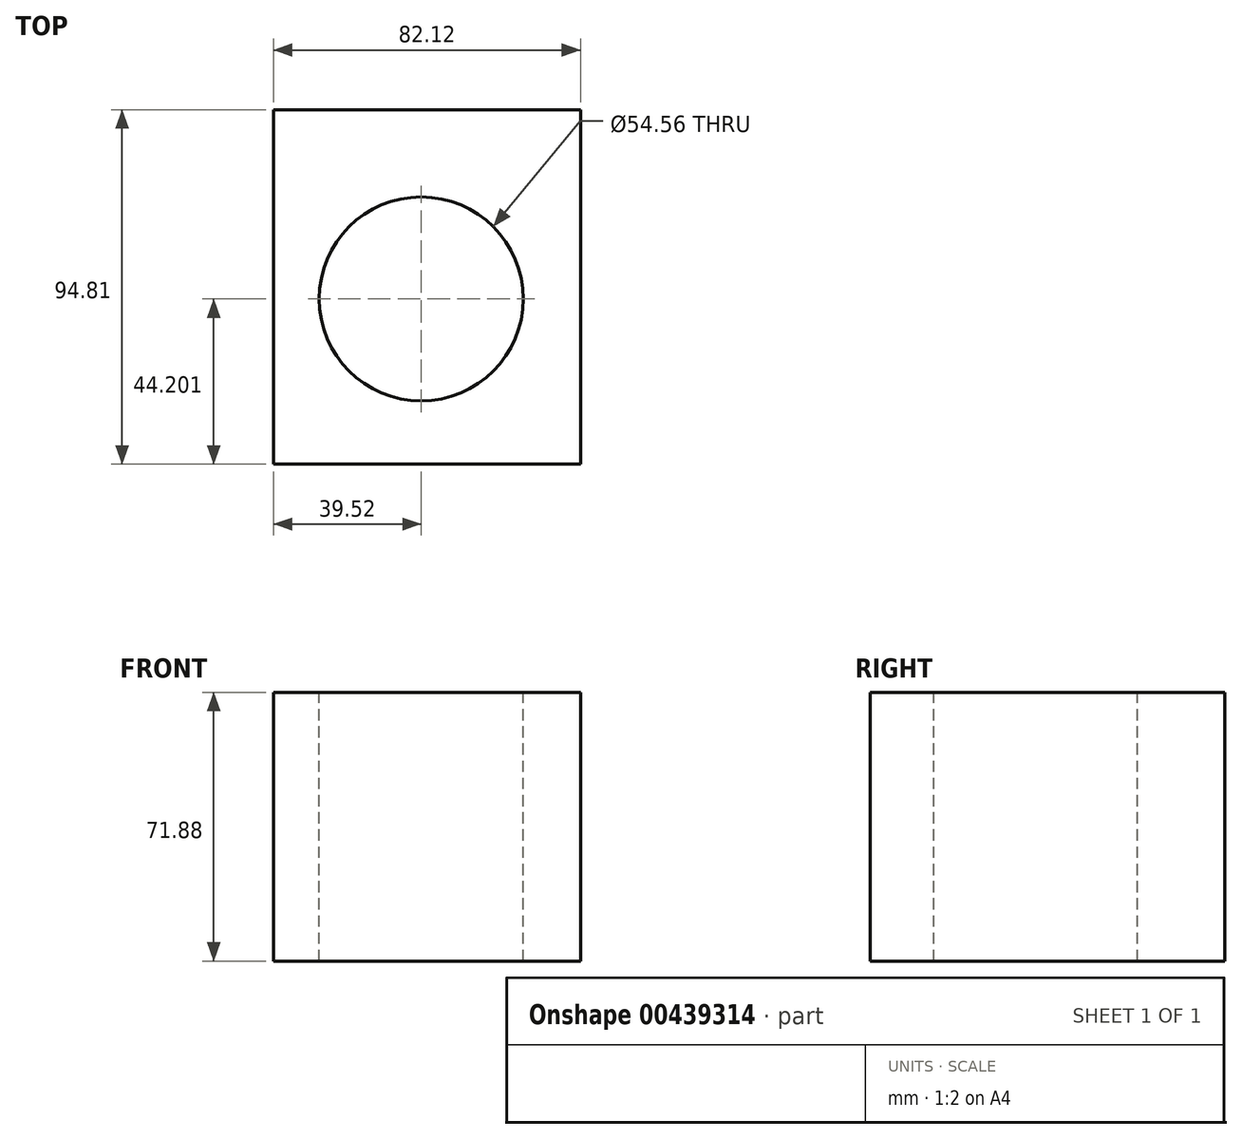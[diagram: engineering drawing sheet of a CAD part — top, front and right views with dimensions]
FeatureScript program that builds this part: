
annotation { "Feature Type Name" : "Feature", "Feature Type Description" : "" }
export const myFeature = defineFeature(function(context is Context, id is Id, definition is map)
    precondition{}
    {
        {
            var Q0;
            Q0=qCreatedBy(makeId("Top.planeOp"),FACE);
            var sketch = newSketch(context, id + "F0", { "sketchPlane" : qUnion([Q0])});
            skLineSegment(sketch, "E0.bottom", {"start": v(0, 0) * mm, "end": v(82.12, 0) * mm});
            skLineSegment(sketch, "E0.top", {"start": v(0, 94.81) * mm, "end": v(82.12, 94.81) * mm});
            skLineSegment(sketch, "E0.left", {"start": v(0, 0) * mm, "end": v(0, 94.81) * mm});
            skLineSegment(sketch, "E0.right", {"start": v(82.12, 0) * mm, "end": v(82.12, 94.81) * mm});
            skSolve(sketch);
        }
        {
            var Q0;
            Q0 = qSketchRegion(id + "F0", true);
            extrude(context, id + "F1", {"entities" : qUnion([Q0]), "depth" : 71.88 * mm});
        }
        {
            var Q0;
            Q0=makeQuery(id+"F1.opExtrude","CAP_FACE",FACE,{"disambiguationData":[OSD([sQuery(id+"F0.wireOp",EDGE,"E0.bottom"),sQuery(id+"F0.wireOp",EDGE,"E0.top"),sQuery(id+"F0.wireOp",EDGE,"E0.left"),sQuery(id+"F0.wireOp",EDGE,"E0.right")])],"isStart":false});
            var sketch = newSketch(context, id + "F2", { "sketchPlane" : qUnion([Q0])});
            skSolve(sketch);
        }
        {
            var Q0;
            Q0=makeQuery(id+"F2.imprint","IMPRINT",FACE,{"disambiguationData":[TD([[makeQuery(id+"F2.imprint","IMPRINT",EDGE,{"derivedFrom":makeQuery(id+"F1.opExtrude","CAP_EDGE",EDGE,{"disambiguationData":[OSD([sQuery(id+"F0.wireOp",EDGE,"E0.bottom")])],"isStart":false})}),1.0]])]});
            var sketch = newSketch(context, id + "F3", { "sketchPlane" : qUnion([Q0])});
            skCircle(sketch, "E1", {"center": v(39.52, 44.2) * mm, "radius": 27.28 * mm});
            skSolve(sketch);
        }
        {
            var Q0;
            Q0=makeQuery(id+"F3.imprint","IMPRINT",FACE,{"disambiguationData":[TD([[makeQuery(id+"F3.imprint","IMPRINT",EDGE,{"derivedFrom":sQuery(id+"F3.wireOp",EDGE,"E1")}),1.0]])]});
            var Q1;
            Q1=sQuery(id+"F3.wireOp",EDGE,"E1");
            extrude(context, id + "F4", {"entities" : qUnion([Q0]), "operationType" : NewBodyOperationType.REMOVE, "surfaceEntities" : qUnion([Q1]), "oppositeDirection" : true, "depth" : 91.44 * mm});
        }
    });
